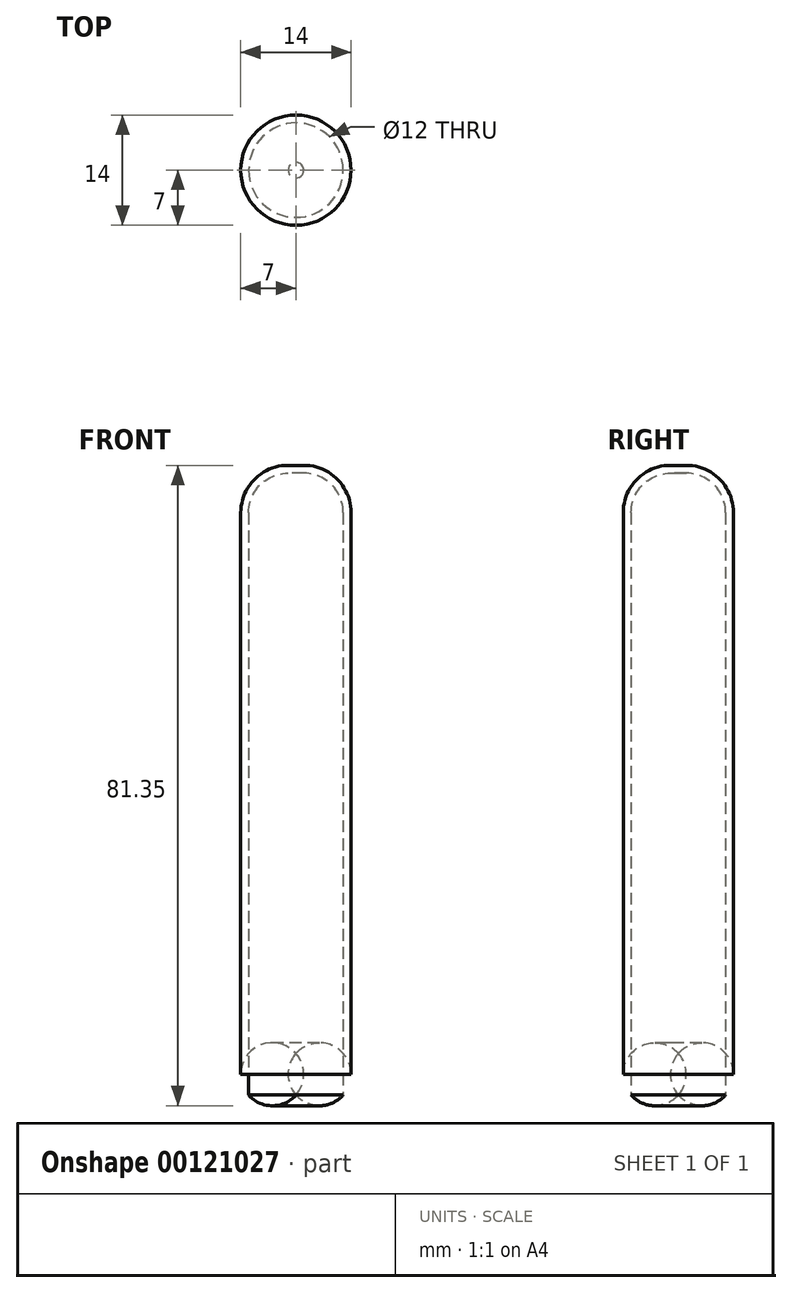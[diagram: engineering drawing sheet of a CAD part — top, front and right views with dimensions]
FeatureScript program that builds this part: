
annotation { "Feature Type Name" : "Feature", "Feature Type Description" : "" }
export const myFeature = defineFeature(function(context is Context, id is Id, definition is map)
    precondition{}
    {
        {
            var Q0;
            Q0=qCreatedBy(makeId("Top.planeOp"),FACE);
            var sketch = newSketch(context, id + "F0", { "sketchPlane" : qUnion([Q0])});
            skCircle(sketch, "E0", {"center": v(0, 0) * mm, "radius": 7 * mm});
            skSolve(sketch);
        }
        {
            var Q0;
            Q0 = qSketchRegion(id + "F0", true);
            extrude(context, id + "F1", {"entities" : qUnion([Q0]), "depth" : 80 * mm});
        }
        {
            var Q0;
            Q0=makeQuery(id+"F1.opExtrude","CAP_EDGE",EDGE,{"disambiguationData":[OSD([sQuery(id+"F0.wireOp",EDGE,"E0")])],"isStart":false});
            fillet(context, id + "F2", {"entities" : qUnion([Q0]), "radius" : 6 * mm, "tangentPropagation" : true, "allowEdgeOverflow" : false});
        }
        {
            var Q0;
            Q0=makeQuery(id+"F1.opExtrude","CAP_FACE",FACE,{"disambiguationData":[OSD([sQuery(id+"F0.wireOp",EDGE,"E0")])],"isStart":true});
            shell(context, id + "F3", {"entities" : qUnion([Q0]), "thickness" : 1 * mm});
        }
        {
            var Q0;
            Q0=makeQuery(id+"F1.opExtrude","CAP_EDGE",EDGE,{"disambiguationData":[OSD([sQuery(id+"F0.wireOp",EDGE,"E0")])],"isStart":true});
            fillet(context, id + "F4", {"entities" : qUnion([Q0]), "radius" : 4 * mm, "tangentPropagation" : true, "allowEdgeOverflow" : false});
        }
    });
